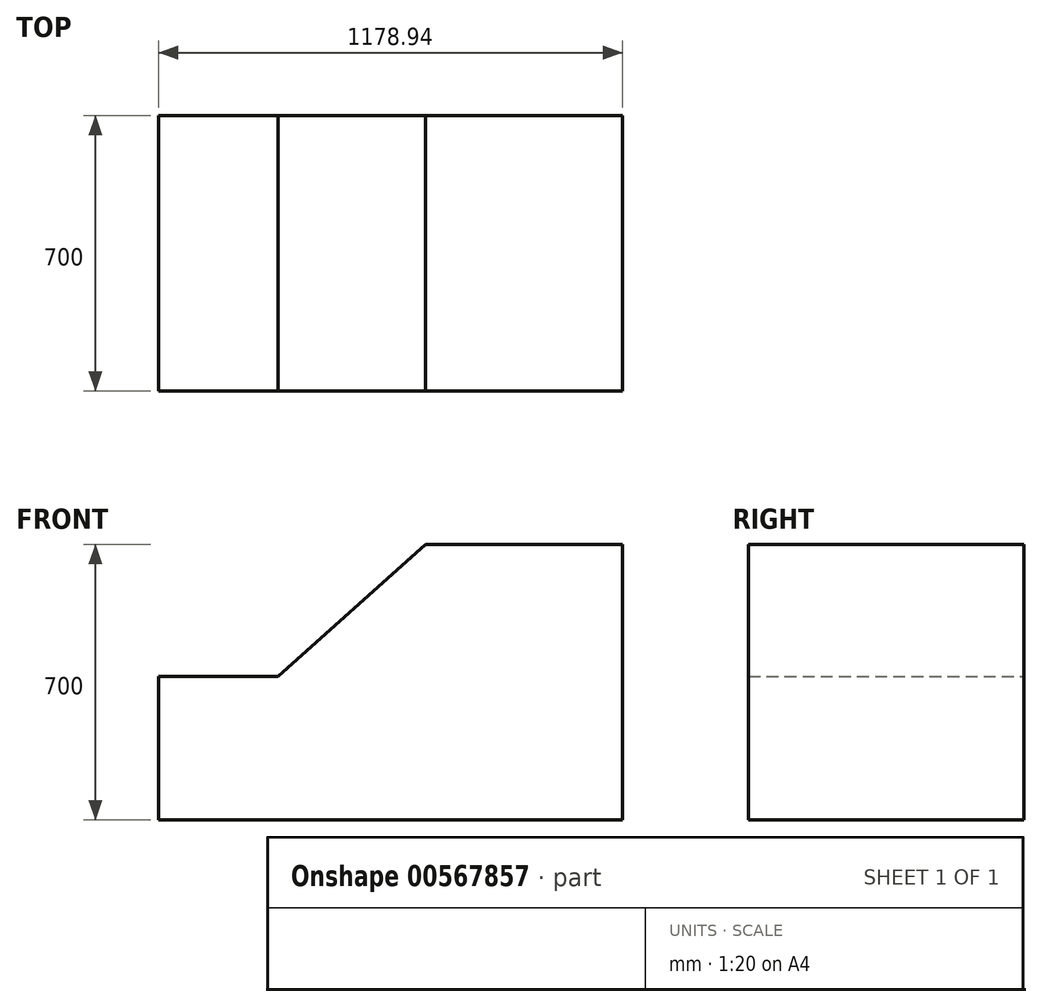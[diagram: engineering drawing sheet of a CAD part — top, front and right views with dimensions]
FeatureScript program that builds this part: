
annotation { "Feature Type Name" : "Feature", "Feature Type Description" : "" }
export const myFeature = defineFeature(function(context is Context, id is Id, definition is map)
    precondition{}
    {
        {
            var Q0;
            Q0=qCreatedBy(makeId("Front.planeOp"),FACE);
            var sketch = newSketch(context, id + "F0", { "sketchPlane" : qUnion([Q0])});
            skLineSegment(sketch, "E0.bottom", {"start": v(-589.47, -350) * mm, "end": v(589.47, -350) * mm});
            skLineSegment(sketch, "E0.top", {"start": v(-589.47, 350) * mm, "end": v(589.47, 350) * mm});
            skLineSegment(sketch, "E0.left", {"start": v(-589.47, -350) * mm, "end": v(-589.47, 350) * mm});
            skLineSegment(sketch, "E0.right", {"start": v(589.47, -350) * mm, "end": v(589.47, 350) * mm});
            skPoint(sketch, "E0.middle", {"position": v(0, 0) * mm});
            skLineSegment(sketch, "E1", {"start": v(589.47, 350) * mm, "end": v(89.47, 350) * mm});
            skLineSegment(sketch, "E2", {"start": v(89.47, 350) * mm, "end": v(-285.77, 14.4) * mm});
            skLineSegment(sketch, "E3", {"start": v(-285.77, 14.4) * mm, "end": v(-683.16, 14.4) * mm});
            skLineSegment(sketch, "E4", {"start": v(-683.16, 14.4) * mm, "end": v(-589.47, 14.4) * mm});
            skLineSegment(sketch, "E5", {"start": v(-589.47, 14.4) * mm, "end": v(-285.77, 14.4) * mm});
            skSolve(sketch);
        }
        {
            var Q0;
            {var subQ1=sQuery(id+"F0.wireOp",EDGE,"E0.bottom");Q0=makeQuery(id+"F0.imprint","IMPRINT",FACE,{"disambiguationData":[TD([[makeQuery(id+"F0.imprint","IMPRINT",EDGE,{"derivedFrom":subQ1}),1.0]])]});}
            extrude(context, id + "F1", {"entities" : qUnion([Q0]), "depth" : 700 * mm, "offsetDistance" : 25.4 * mm});
        }
    });
